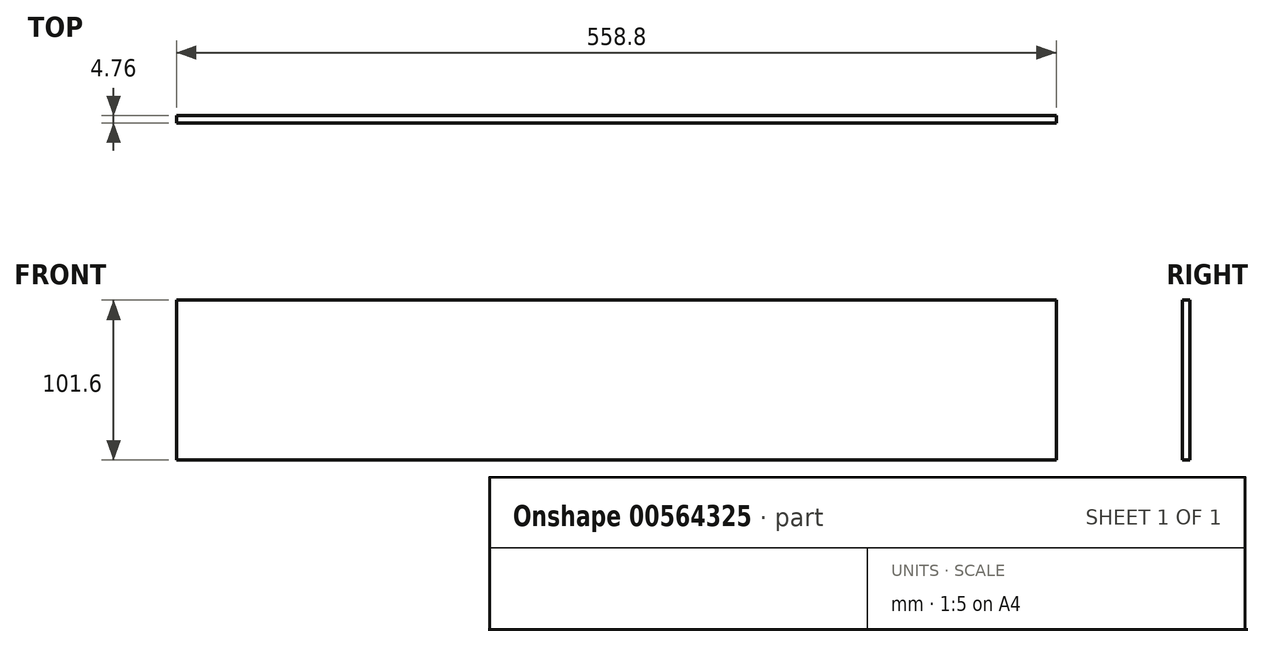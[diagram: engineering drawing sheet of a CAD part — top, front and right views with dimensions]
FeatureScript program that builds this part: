
annotation { "Feature Type Name" : "Feature", "Feature Type Description" : "" }
export const myFeature = defineFeature(function(context is Context, id is Id, definition is map)
    precondition{}
    {
        {
            var Q0;
            Q0=qCreatedBy(makeId("Right.planeOp"),FACE);
            var sketch = newSketch(context, id + "F0", { "sketchPlane" : qUnion([Q0])});
            skLineSegment(sketch, "E0.bottom", {"start": v(-2.38, 50.8) * mm, "end": v(2.38, 50.8) * mm});
            skLineSegment(sketch, "E0.top", {"start": v(-2.38, -50.8) * mm, "end": v(2.38, -50.8) * mm});
            skLineSegment(sketch, "E0.left", {"start": v(-2.38, 50.8) * mm, "end": v(-2.38, -50.8) * mm});
            skLineSegment(sketch, "E0.right", {"start": v(2.38, 50.8) * mm, "end": v(2.38, -50.8) * mm});
            skPoint(sketch, "E0.middle", {"position": v(0, 0) * mm});
            skSolve(sketch);
        }
        {
            var Q0;
            Q0 = qSketchRegion(id + "F0", true);
            extrude(context, id + "F1", {"entities" : qUnion([Q0]), "endBound" : BoundingType.SYMMETRIC, "depth" : 558.8 * mm, "offsetDistance" : 25.4 * mm});
        }
    });
